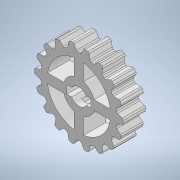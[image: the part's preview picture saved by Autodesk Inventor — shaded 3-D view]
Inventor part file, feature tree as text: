
AUTODESK INVENTOR PART (.ipt)
format: ipt  version: 2022 (Build 260153000, 153)  size: 467,456 bytes
history: native  units: mm
features: extrude x4, sketch x4, other x4, reference x2, plane x1, projected_geometry x1
ambient origin geometry x8: Origin, YZ Plane, XZ Plane, XY Plane, X Axis, Y Axis, Z Axis, Center Point
bodies: Solid1 (feature_tree)
feature tree (16):
  extrude  "Extrusion1"  Depth=10.0mm
  sketch  "Sketch2"  dims[d2=2.0mm d3=5.0mm d4=0.0mm d5=0.0mm d6=40.0mm d8=360.0deg]
  plane  "Work Plane1"
  extrude  "Extrusion2"  Depth=5.0mm TaperAngle=360.0deg
  extrude  "Extrusion3"  TaperAngle=0.0deg  [1 undecoded]
  extrude  "Extrusion4"  Depth=10.0mm
  sketch  "Sketch1"  dims[d0=10.0mm d1=0.3mm]
  reference  "Reference1"
  projected_geometry  "Projected Loop1"
  sketch  "Sketch3"  dims[d10=2.0mm d11=0.0mm d12=0.0mm d13=0.0mm]
  sketch  "Sketch4"  dims[d14=33.0mm d15=29.0mm d16=2.0mm d17=2.0mm d18=3.0mm d19=40.0mm d21=360.0deg d23=1.5mm d24=3.0mm d25=0.5mm d26=0.5mm d27=180.0mm d29=360.0deg d31=10.0mm d32=0.0mm]
  reference  "Reference2"
  other  "<userpath>\OneDrive - Imperial College London\ROBOICP\new vial holder assembly.iam"
  other  "new vial holder assembly.iam"
  other  "Mixer:1"
  other  "mixer_gear:5"
note: 1 required parameter value undecoded (feature->parameter linkage not recoverable at this tier; creation-order binding heuristic only, values carry confidence <= 0.55)
